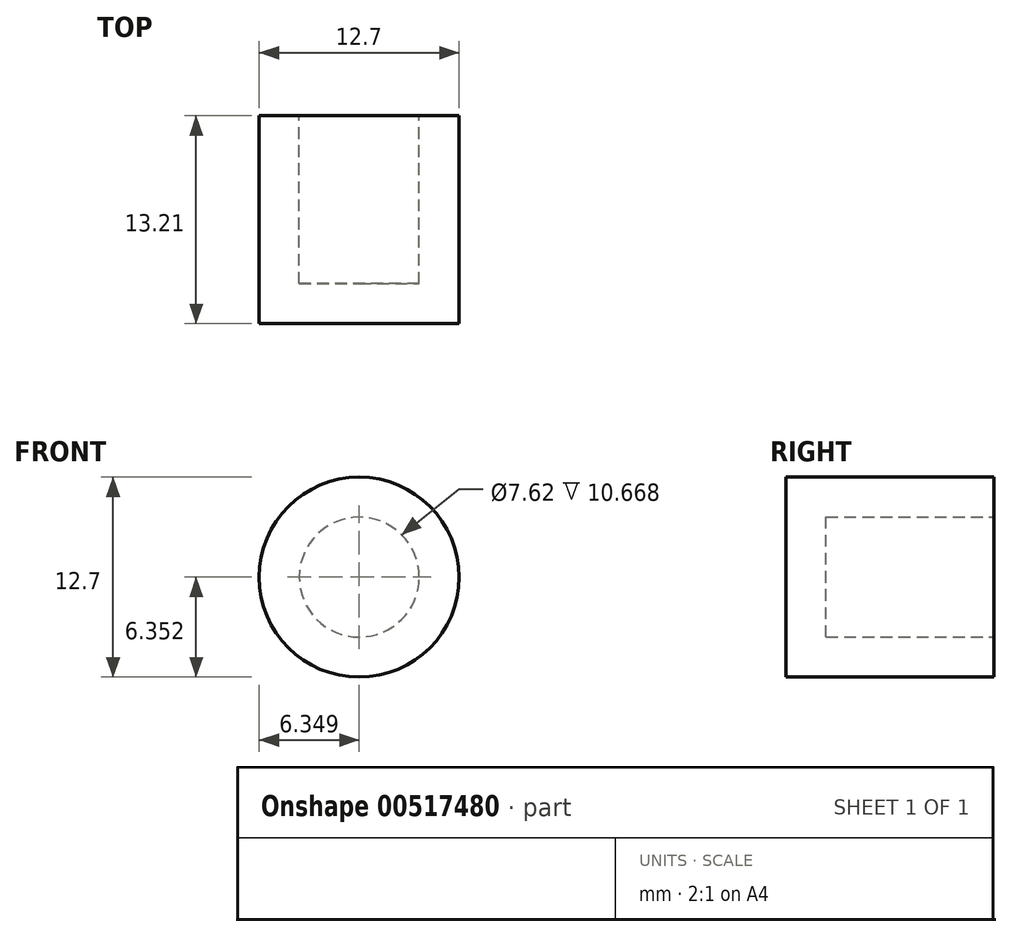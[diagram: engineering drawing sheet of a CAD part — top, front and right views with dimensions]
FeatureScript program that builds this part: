
annotation { "Feature Type Name" : "Feature", "Feature Type Description" : "" }
export const myFeature = defineFeature(function(context is Context, id is Id, definition is map)
    precondition{}
    {
        {
            var Q0;
            Q0=qCreatedBy(makeId("Front.planeOp"),FACE);
            var sketch = newSketch(context, id + "F0", { "sketchPlane" : qUnion([Q0])});
            skCircle(sketch, "E0", {"center": v(-10.05, 14) * mm, "radius": 6.35 * mm});
            skSolve(sketch);
        }
        {
            var Q0;
            Q0=makeQuery(id+"F0.imprint","IMPRINT",FACE,{"disambiguationData":[TD([[makeQuery(id+"F0.imprint","IMPRINT",EDGE,{"derivedFrom":sQuery(id+"F0.wireOp",EDGE,"E0")}),1.0]])]});
            extrude(context, id + "F1", {"entities" : qUnion([Q0]), "depth" : 13.2 * mm, "offsetDistance" : 25.4 * mm});
        }
        {
            var Q0;
            Q0=makeQuery(id+"F1.opExtrude","CAP_FACE",FACE,{"disambiguationData":[OSD([sQuery(id+"F0.wireOp",EDGE,"E0")])],"isStart":true});
            shell(context, id + "F2", {"entities" : qUnion([Q0]), "thickness" : 2.54 * mm});
        }
    });
